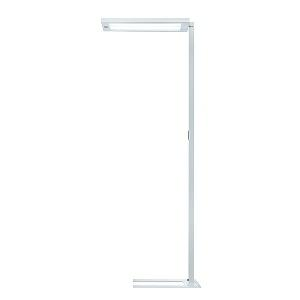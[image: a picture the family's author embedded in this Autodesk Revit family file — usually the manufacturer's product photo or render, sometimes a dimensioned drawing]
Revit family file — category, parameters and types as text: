
# Revit family: lavigo_-_dps_16500_840_r_g2_00804523_2ab8
name_source: partatom
category: Lighting Fixtures
units: mm (PartAtom-declared; Revit-internal decimal feet)

## family parameters
Cut with Voids When Loaded = No
Host = Face
Light Source = No
Part Type = Normal
Room Calculation Point = No
Round Connector Dimension = Use Diameter
Shared = No

## types (1)
- LAVIGO - DPS 16500/840/R/G2 (1 x LED, 16150 lm, 4000K)
    Apparent Load = 113 VA
    Approval mark = CE
    CIE Flux Codes = 60 87 97 11 100
    Color Rendering = 80-89
    Color Temperature = 4000K
    Control Gear = Electronic ballast
    Default Elevation = 1800 mm
    Description = DPS 16500/840/R/G2|Free-standing luminaire|light source: LED|work equipment: Electronic ballast|connected load: 220-240 V, 50/60 Hz|Power consumption: approx. 113 W|standby: approx. 0,50|power factor: approx. 0,963|luminous flux: 16150 lm|luminous efficacy: 142 lm/W|light distribution: Direct/indirect|direct ratio: approx. 11 %|colour temperature: Cold white, ca. 4000 K|color rendering index (CRI): >= 80|chromaticity tolerance:  3 SDCM|technology: Presence and daylight sensor control (PIR)|operation: Multi-function switch|luminaire body|material: Steel/plastic|surface: Painted|colour: White|lamp cover: Acrylic (PMMA), Satine|tubular section|material: Steel tube|surface: Painted|Form: Tubular section upright|colour of tubular section: White|luminaire base|Form: C-form flat|weight (net): approx. 19.7 kg|mains lead: 3.00 m Mains plug CEE 7/VII|Fastening: Floor standing base|decorative contrast side parts: Flint grey|glare control: Prism aperture|luminance(L65): <= 3000 cd/m|unified glare rating(4H 8H): <=  16|special features: Luminaire head detachable, Cradle to Cradle Certified TM, Direct light component with edge light and light-guide technology for homogenous light exit, Flicker-free, Integrated light and presence sensor PIR, Retrofittable with TALK module, Separated, direct and indirect light individually adjustable|Approval mark: VDE - ENEC|
    Frequency = 50 Hz, 60 Hz
    Height = 36 mm
    Lamp = 1 x LED
    Lamp Light Flux = 16150 lm
    Lamp count = 1
    Length = 675 mm
    Luminous efficacy = 143 lm/W
    Manufacturer = Waldmann
    ModVariant = No
    Model = 00804523
    Mounting Place = Floor
    Mounting Type = Freestanding
    Number of Poles = 1
    OnlyDefault = Yes
    Power Factor = 1
    Product Name = LAVIGO - DPS 16500/840/R/G2
    Product group = Free standing luminaire
    ProductGroupID = 13
    Protection Class = Protection class I
    Protection Degree = IP 20
    RLX_Detail_Level = 1
    RLX_Emergency_Light_Flux = 0 lm
    RLX_Emergency_Type = 0
    RLX_Emergency_Type_DB = No
    RlxData = <blob elided: 36893 chars, md5=39f0cea4>
    Socket = socket
    Standby Power = 0 W
    System Light Flux = 16150 lm
    System Power = 113 W
    Type Comments = Product without accessories
    Type Image = 121695000-00610208.jpg
    URL = http://relux.com
    VarID = ---
    Voltage = 230 V
    Voltage Range = 220-240 V
    Weight = 0.00 kg
    Width = 320 mm

## geometry (parser evidence)
native form markers: Blend x4, Sweep x16
no freeform markers — native parametric forms only
